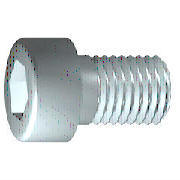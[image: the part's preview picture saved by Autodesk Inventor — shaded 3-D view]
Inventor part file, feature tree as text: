
AUTODESK INVENTOR PART (.ipt)
format: ipt  version: 2022 (Build 260153000, 153)  size: 196,096 bytes
history: native  units: mm (DEFAULTED — no unit token found)
features: sketch x2, other x1, extrude x1, plane x1, fillet x1
ambient origin geometry x7: Origin, YZ Plane, XY Plane, X Axis, Y Axis, Z Axis, Center Point
bodies: Solid1 (feature_tree)
feature tree (6):
  other  "Базовый элемент"
  extrude  "Паз"  Depth=7.9mm
  plane  "Work Plane1"
  fillet  "Fillet2"  Radius=0.429515mm
  sketch  "Эскиз1"
  sketch  "Эскиз2"
